# Revit family: Storage-Teknion-LWBTH_Byward_High_Tower-R2019
name_source: partatom
category: Furniture
units: mm (PartAtom-declared; Revit-internal decimal feet)

## family parameters
Always vertical = Yes
Cut with Voids When Loaded = No
OmniClass Number = 23.40.20.00
OmniClass Title = General Furniture and Specialties
Room Calculation Point = No
Shared = Yes
Work Plane-Based = No

## types (5) — shared parameters
Assembly Code = E2020200
Manufacturer = Teknion
Manufacturer Fax = 416.661.4586
Part Number = LWBTH
Product Documentation Link = https://assets.teknion.com
Product Line = Byward
Product Page URL = https://www.teknion.com
Series = Byward
Sustainability Data = https://www.teknion.com
URL = www.teknion.com
Unit Weight URL = http://www.teknion.com
Warranty = http://www.teknion.com

## per-type parameters (varying)
| type | 2D Coat Divider Left | 2D Coat Divider Right | 2D Coat Lines | All Closed | Description | Left Coat Door | Left Coat, Right Open Cut Depth | Left Open, Right Coat Cut Depth | Model | Plan View Shelf Depth Cut Depth | Right Coat Door |
| Left Coat, Right Open | Yes | No | Yes | 0.5 " | Byward High Tower, Left Coat, Right Open, 60" Height, 14" Depth | Yes | 16.563 " | 0.5 " | LWBTHJO6014__ | 62.5 " | No |
| Left Open, Right Coat | No | Yes | Yes | 0.5 " | Byward High Tower, Left Open, Right Coat, 60" Height, 14" Depth | No | 0.5 " | 16.563 " | LWBTHOJ6014__ | 62.5 " | Yes |
| All Closed | No | No | No | 16.563 " | Byward High Tower, All Closed, 60" Height, 14" Depth | Yes | 0.5 " | 0.5 " | LWBTHCC6014__ | 0.5 " | Yes |
| Left Closed, Right Coat | No | Yes | Yes | 0.5 " | Byward High Tower, Left Closed, Right Coat, 60" Height, 14" Depth | Yes | 0.5 " | 16.563 " | LWBTHCJ6014__ | 0.5 " | Yes |
| All Open | No | No | No | 16.563 " | Byward High Tower, All Open, 60" Height, 14" Depth | No | 0.5 " | 0.5 " | LWBTHOO6014__ | 0.5 " | No |

## geometry (parser evidence)
native form markers: Sweep x6
no freeform markers — native parametric forms only
